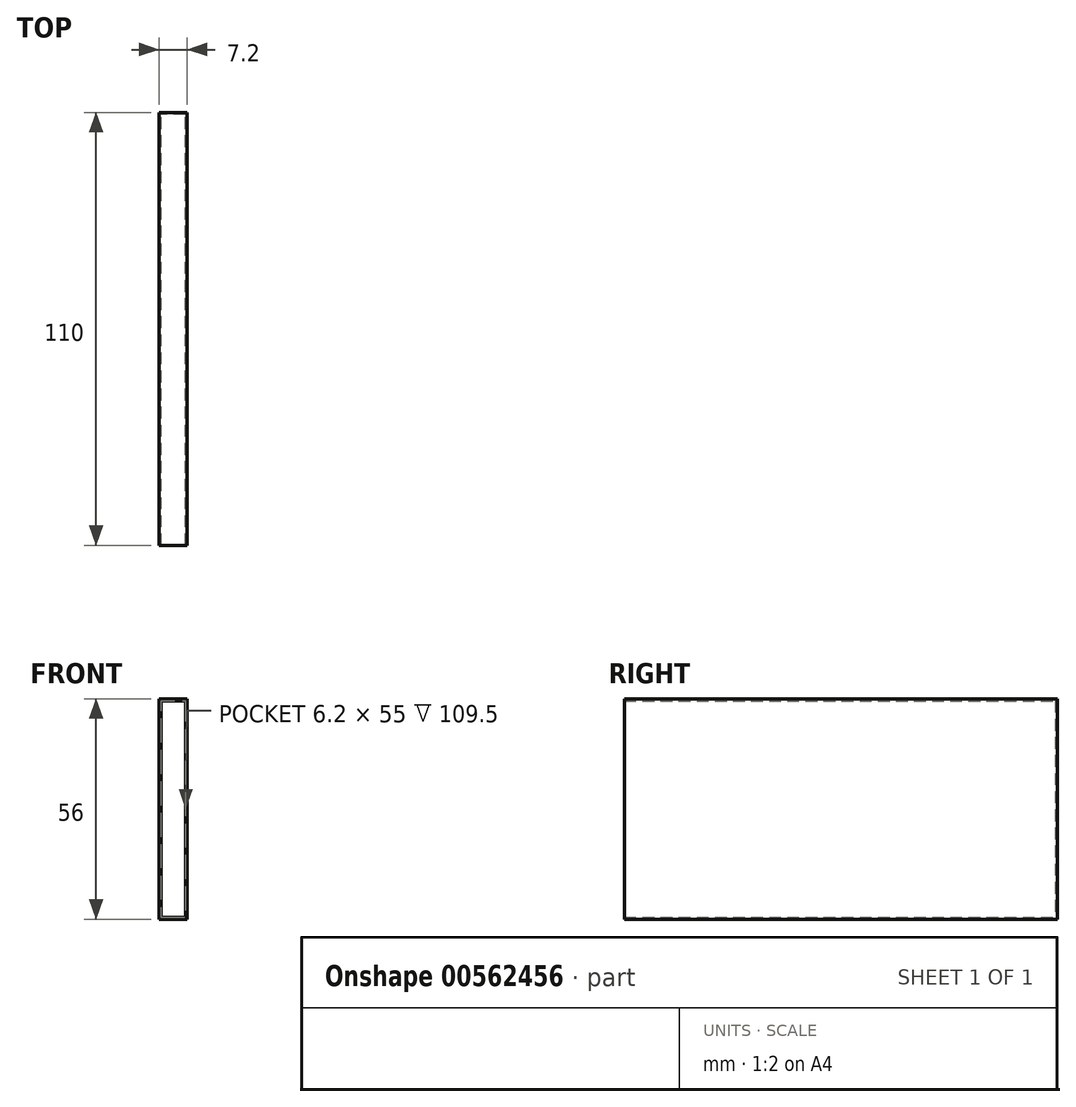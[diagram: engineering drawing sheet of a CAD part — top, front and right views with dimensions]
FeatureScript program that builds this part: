
annotation { "Feature Type Name" : "Feature", "Feature Type Description" : "" }
export const myFeature = defineFeature(function(context is Context, id is Id, definition is map)
    precondition{}
    {
        {
            var Q0;
            Q0=qCreatedBy(makeId("Right.planeOp"),FACE);
            var sketch = newSketch(context, id + "F0", { "sketchPlane" : qUnion([Q0])});
            skLineSegment(sketch, "E0.bottom", {"start": v(-55, 28) * mm, "end": v(55, 28) * mm});
            skLineSegment(sketch, "E0.top", {"start": v(-55, -28) * mm, "end": v(55, -28) * mm});
            skLineSegment(sketch, "E0.left", {"start": v(-55, 28) * mm, "end": v(-55, -28) * mm});
            skLineSegment(sketch, "E0.right", {"start": v(55, 28) * mm, "end": v(55, -28) * mm});
            skPoint(sketch, "E0.middle", {"position": v(0, 0) * mm});
            skSolve(sketch);
        }
        {
            var Q0;
            Q0=makeQuery(id+"F0.imprint","IMPRINT",FACE,{"disambiguationData":[TD([[makeQuery(id+"F0.imprint","IMPRINT",EDGE,{"derivedFrom":sQuery(id+"F0.wireOp",EDGE,"E0.bottom")}),-1.0]])]});
            extrude(context, id + "F1", {"entities" : qUnion([Q0]), "depth" : 7.2 * mm, "offsetDistance" : 25 * mm, "symmetric" : true});
        }
        {
            var Q0;
            Q0=makeQuery(id+"F1.opExtrude","SWEPT_FACE",FACE,{"disambiguationData":[OSD([sQuery(id+"F0.wireOp",EDGE,"E0.left")])]});
            shell(context, id + "F2", {"entities" : qUnion([Q0]), "thickness" : .5 * mm});
        }
    });
